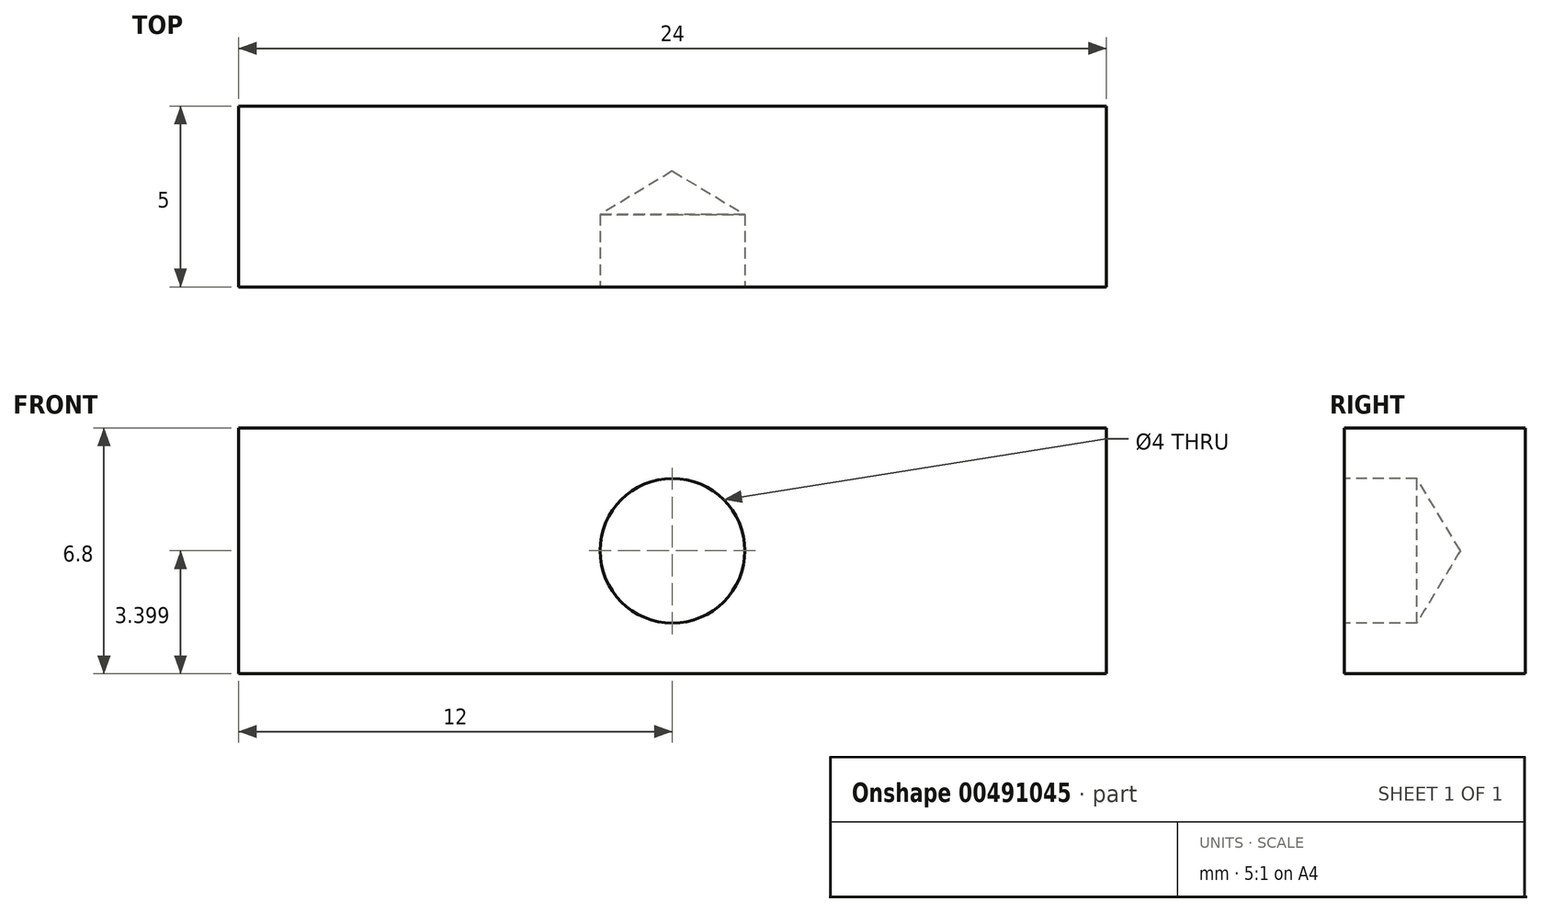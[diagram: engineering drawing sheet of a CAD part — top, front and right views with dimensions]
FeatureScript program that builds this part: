
annotation { "Feature Type Name" : "Feature", "Feature Type Description" : "" }
export const myFeature = defineFeature(function(context is Context, id is Id, definition is map)
    precondition{}
    {
        {
            var Q0;
            Q0=qCreatedBy(makeId("Front.planeOp"),FACE);
            var sketch = newSketch(context, id + "F0", { "sketchPlane" : qUnion([Q0])});
            skLineSegment(sketch, "E0.bottom", {"start": v(-12, 67.4) * mm, "end": v(12, 67.4) * mm});
            skLineSegment(sketch, "E0.top", {"start": v(-12, 60.6) * mm, "end": v(12, 60.6) * mm});
            skLineSegment(sketch, "E0.left", {"start": v(-12, 67.4) * mm, "end": v(-12, 60.6) * mm});
            skLineSegment(sketch, "E0.right", {"start": v(12, 67.4) * mm, "end": v(12, 60.6) * mm});
            skSolve(sketch);
        }
        {
            var Q0;
            Q0=makeQuery(id+"F0.imprint","IMPRINT",FACE,{"disambiguationData":[TD([[makeQuery(id+"F0.imprint","IMPRINT",EDGE,{"derivedFrom":sQuery(id+"F0.wireOp",EDGE,"E0.bottom")}),-1.0]])]});
            extrude(context, id + "F1", {"entities" : qUnion([Q0]), "depth" : 5 * mm, "offsetDistance" : 25 * mm});
        }
        {
            var Q0;
            Q0=makeQuery(id+"F1.opExtrude","CAP_FACE",FACE,{"disambiguationData":[OSD([sQuery(id+"F0.wireOp",EDGE,"E0.bottom"),sQuery(id+"F0.wireOp",EDGE,"E0.top"),sQuery(id+"F0.wireOp",EDGE,"E0.left"),sQuery(id+"F0.wireOp",EDGE,"E0.right")])],"isStart":false});
            var sketch = newSketch(context, id + "F2", { "sketchPlane" : qUnion([Q0])});
            skCircle(sketch, "E1", {"center": v(0, 64) * mm, "radius": 2 * mm});
            skPoint(sketch, "E1.centerSnap0", {"position": v(0, 67.4) * mm});
            skSolve(sketch);
        }
        {
            var Q0;
            Q0=sQuery(id+"F2.wireOp",VERTEX,"E1.center");
            var Q1;
            Q1=makeQuery(id+"F1.opExtrude","SWEPT_BODY",BODY,{"disambiguationData":[OSD([sQuery(id+"F0.wireOp",EDGE,"E0.bottom"),sQuery(id+"F0.wireOp",EDGE,"E0.top"),sQuery(id+"F0.wireOp",EDGE,"E0.left"),sQuery(id+"F0.wireOp",EDGE,"E0.right")])]});
            hole(context, id + "F3", {"style" : HoleStyle.SIMPLE, "endStyle" : HoleEndStyle.BLIND, "holeDiameter" : 4 * mm, "holeDepth" : 2 * mm, "isTappedThrough" : true, "tappedDepth" : 12 * mm, "tapClearance" : 3, "locations" : qUnion([Q0]), "scope" : qUnion([Q1])});
        }
    });
